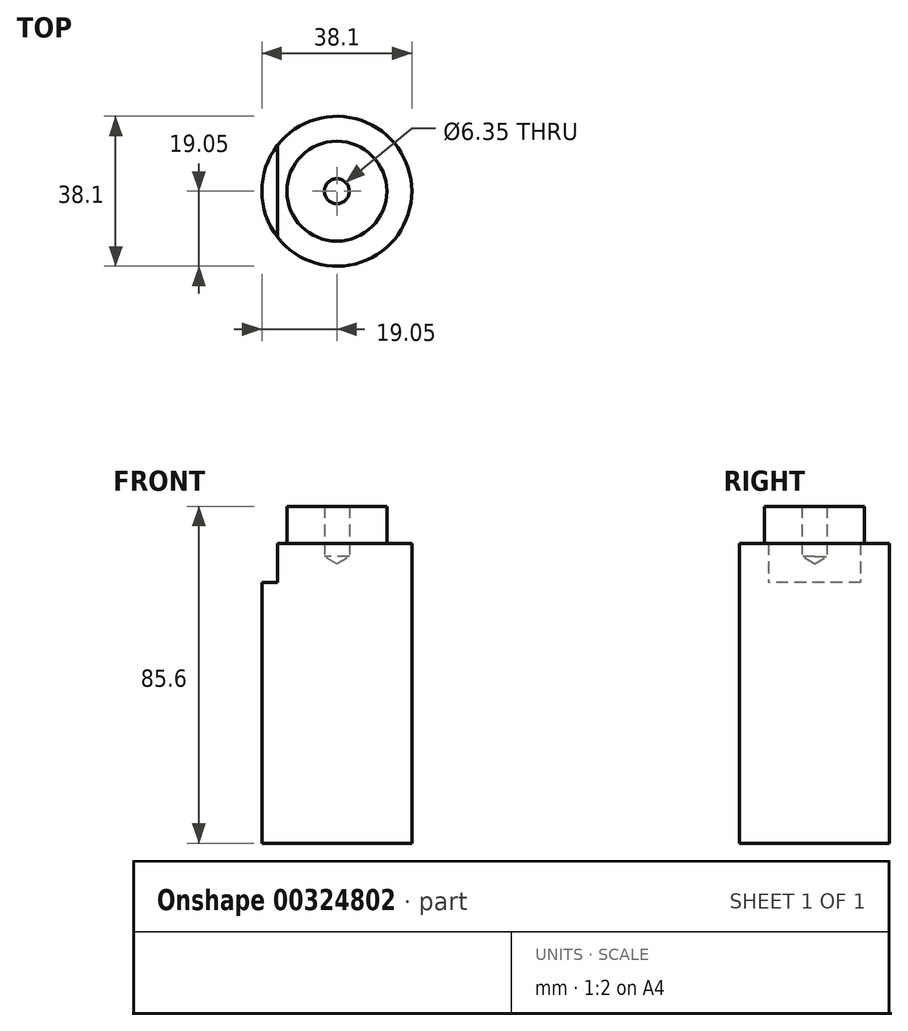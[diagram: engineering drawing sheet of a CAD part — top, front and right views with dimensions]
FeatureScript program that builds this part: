
annotation { "Feature Type Name" : "Feature", "Feature Type Description" : "" }
export const myFeature = defineFeature(function(context is Context, id is Id, definition is map)
    precondition{}
    {
        {
            var Q0;
            Q0=qCreatedBy(makeId("Top.planeOp"),FACE);
            var sketch = newSketch(context, id + "F0", { "sketchPlane" : qUnion([Q0])});
            skCircle(sketch, "E0", {"center": v(0, 0) * mm, "radius": 19.05 * mm});
            skSolve(sketch);
        }
        {
            var Q0;
            Q0=makeQuery(id+"F0.imprint","IMPRINT",FACE,{"disambiguationData":[TD([[makeQuery(id+"F0.imprint","IMPRINT",EDGE,{"derivedFrom":sQuery(id+"F0.wireOp",EDGE,"E0")}),1.0]])]});
            extrude(context, id + "F1", {"entities" : qUnion([Q0]), "depth" : 76.2 * mm, "offsetDistance" : 25.4 * mm});
        }
        {
            var Q0;
            Q0=makeQuery(id+"F1.opExtrude","CAP_FACE",FACE,{"disambiguationData":[OSD([sQuery(id+"F0.wireOp",EDGE,"E0")])],"isStart":false});
            var sketch = newSketch(context, id + "F2", { "sketchPlane" : qUnion([Q0])});
            skCircle(sketch, "E1", {"center": v(0, 0) * mm, "radius": 12.7 * mm});
            skSolve(sketch);
        }
        {
            var Q0;
            Q0=makeQuery(id+"F2.imprint","IMPRINT",FACE,{"disambiguationData":[TD([[makeQuery(id+"F2.imprint","IMPRINT",EDGE,{"derivedFrom":sQuery(id+"F2.wireOp",EDGE,"E1")}),1.0]])]});
            extrude(context, id + "F3", {"entities" : qUnion([Q0]), "operationType" : NewBodyOperationType.ADD, "depth" : 9.4 * mm, "offsetDistance" : 25.4 * mm});
        }
        {
            var Q0;
            Q0=makeQuery(id+"F3.opExtrude","CAP_FACE",FACE,{"disambiguationData":[OSD([sQuery(id+"F2.wireOp",EDGE,"E1")])],"isStart":false});
            var sketch = newSketch(context, id + "F4", { "sketchPlane" : qUnion([Q0])});
            skLineSegment(sketch, "E2", {"start": v(-15.04, 26.06) * mm, "end": v(-15.04, -12.65) * mm, "construction": true});
            skLineSegment(sketch, "E3", {"start": v(-15.04, 12.65) * mm, "end": v(-15.04, -12.65) * mm});
            skArc(sketch, "E4", {"start": v(-15.04, 12.65) * mm, "mid": v(-19.65, 0) * mm, "end": v(-15.04, -12.65) * mm});
            skLineSegment(sketch, "E5.trimOffspring", {"start": v(-15.04, -13.9) * mm, "end": v(-15.04, -24.28) * mm, "construction": true});
            skSolve(sketch);
        }
        {
            var Q0;
            Q0=makeQuery(id+"F4.imprint","IMPRINT",FACE,{"disambiguationData":[TD([[makeQuery(id+"F4.imprint","IMPRINT",EDGE,{"derivedFrom":sQuery(id+"F4.wireOp",EDGE,"E3")}),-1.0]])]});
            extrude(context, id + "F5", {"entities" : qUnion([Q0]), "operationType" : NewBodyOperationType.REMOVE, "oppositeDirection" : true, "depth" : 19.3 * mm, "offsetDistance" : 25.4 * mm});
        }
        {
            var Q0;
            Q0=makeQuery(id+"F3.opExtrude","CAP_FACE",FACE,{"disambiguationData":[OSD([sQuery(id+"F2.wireOp",EDGE,"E1")])],"isStart":false});
            var sketch = newSketch(context, id + "F6", { "sketchPlane" : qUnion([Q0])});
            skPoint(sketch, "E6", {"position": v(0, 0) * mm});
            skSolve(sketch);
        }
        {
            var Q0;
            Q0=sQuery(id+"F6.wireOp",VERTEX,"E6");
            var Q1;
            Q1=makeQuery(id+"F1.opExtrude","SWEPT_BODY",BODY,{"disambiguationData":[OSD([sQuery(id+"F0.wireOp",EDGE,"E0")])]});
            hole(context, id + "F7", {"style" : HoleStyle.SIMPLE, "endStyle" : HoleEndStyle.BLIND, "holeDiameter" : 6.35 * mm, "majorDiameter" : 6.35 * mm, "holeDepth" : 12.7 * mm, "tappedDepth" : 12.7 * mm, "tapClearance" : 3, "locations" : qUnion([Q0]), "scope" : qUnion([Q1])});
        }
    });
